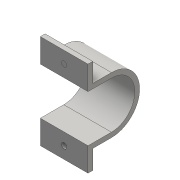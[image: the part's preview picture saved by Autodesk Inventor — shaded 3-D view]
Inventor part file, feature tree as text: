
AUTODESK INVENTOR PART (.ipt)
format: ipt  version: 2016 (Build 200138000, 138)  size: 115,200 bytes
history: native  units: mm
features: extrude x2, sketch x2
ambient origin geometry x8: Origin, YZ Plane, XZ Plane, XY Plane, X Axis, Y Axis, Z Axis, Center Point
bodies: Solid1 (feature_tree)
feature tree (4):
  extrude  "Extrusion1"  Depth=2.54mm
  extrude  "Extrusion2"  Depth=12.7mm
  sketch  "Sketch1"  dims[d0=25.0mm d1=2.54mm d2=2.54mm d6=12.5mm]
  sketch  "Sketch2"  dims[d9=12.7mm d10=12.7mm d11=2.54mm d12=2.54mm d15=2.54mm d17=0.006361mm d23=0.0mm d24=0.0mm d25=0.0mm d26=0.0mm d27=0.04mm d28=4.98mm d29=25.4mm d30=0.0mm d31=2.8448mm d32=6.35mm d33=12.7mm d34=0.0mm d35=6.35mm d36=2.8448mm d37=25.4mm d38=0.0mm]
